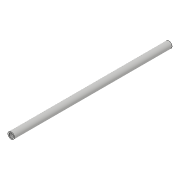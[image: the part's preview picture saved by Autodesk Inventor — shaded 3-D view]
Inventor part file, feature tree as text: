
AUTODESK INVENTOR PART (.ipt)
format: ipt  version: 2018.3 (Build 223284000, 284)  size: 82,944 bytes
history: native  units: in
note: dims shown in document units (in); Inventor stores cm internally (conversion verified against a paired STEP export)
features: sketch x3, hole x2, extrude x1
ambient origin geometry x8: Origin, YZ Plane, XZ Plane, XY Plane, X Axis, Y Axis, Z Axis, Center Point
bodies: Solid1 (feature_tree)
feature tree (6):
  extrude  "Extrusion1"  Depth=3.0in TaperAngle=0.0deg
  hole  "Hole1"  [1 undecoded]
  hole  "Hole2"  [1 undecoded]
  sketch  "Sketch1"  dims[d0=0.125in d1=3.0in d2=0.0in]
  sketch  "Sketch2"  dims[d3=0.089in]
  sketch  "Sketch3"  dims[d4=0.085in d5=0.75in d6=0.375in d7=0.25in d8=0.5635in d9=1.0in d10=0.8108in d11=0.085in d12=0.75in d13=0.375in d14=0.25in d15=0.5635in d16=1.0in d17=0.8108in]
note: 2 required parameter values undecoded (feature->parameter linkage not recoverable at this tier; creation-order binding heuristic only, values carry confidence <= 0.55)
